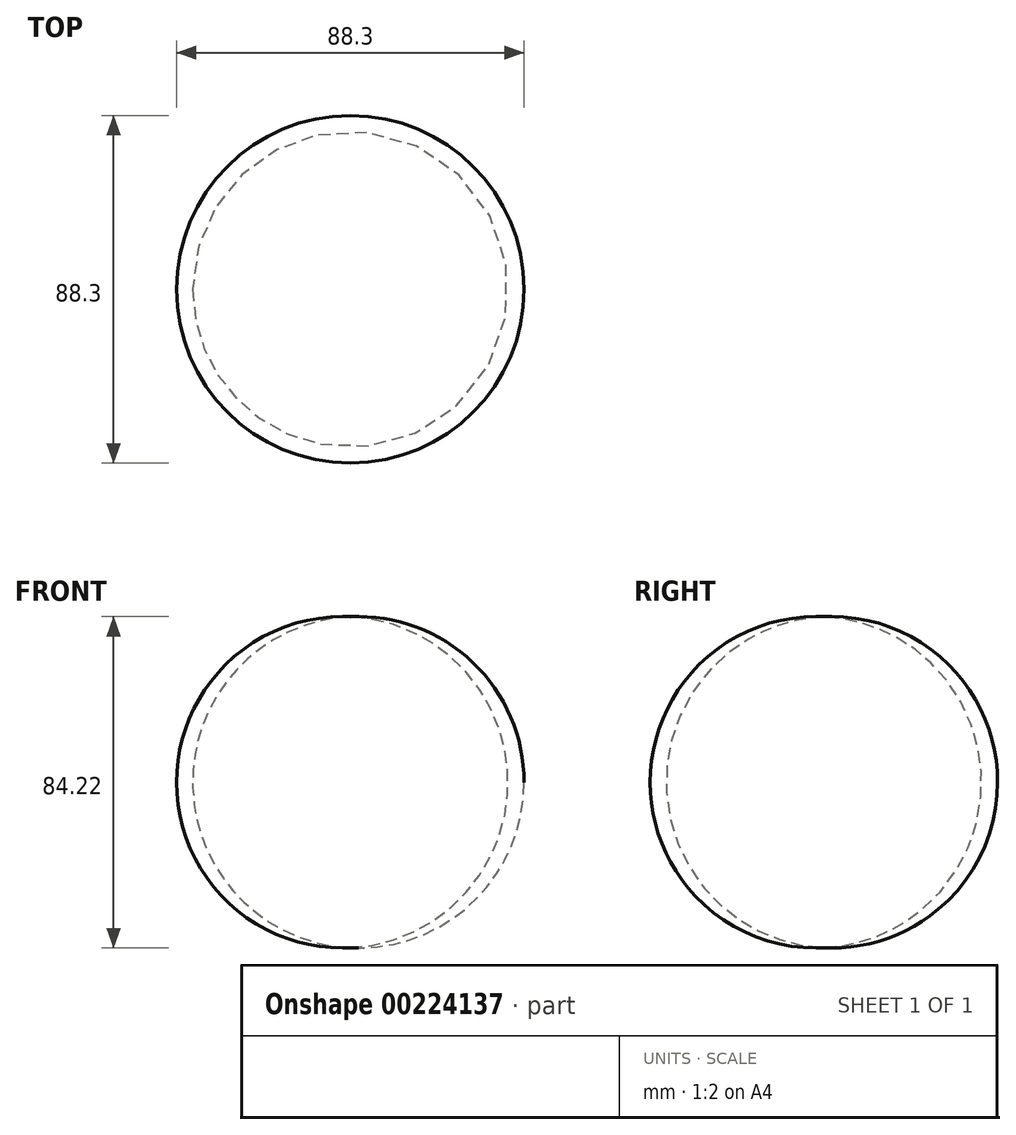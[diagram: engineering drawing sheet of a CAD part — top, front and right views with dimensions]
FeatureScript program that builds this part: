
annotation { "Feature Type Name" : "Feature", "Feature Type Description" : "" }
export const myFeature = defineFeature(function(context is Context, id is Id, definition is map)
    precondition{}
    {
        {
            var Q0;
            Q0=qCreatedBy(makeId("Front.planeOp"),FACE);
            var sketch = newSketch(context, id + "F0", { "sketchPlane" : qUnion([Q0])});
            skCircle(sketch, "E0", {"center": v(2.04, 0) * mm, "radius": 42.1 * mm});
            skLineSegment(sketch, "E1", {"start": v(0, 42.06) * mm, "end": v(0, -42.06) * mm});
            skSolve(sketch);
        }
        {
            var Q0;
            {var subQ0=sQuery(id+"F0.wireOp",EDGE,"E1");Q0=makeQuery(id+"F0.imprint","IMPRINT",FACE,{"disambiguationData":[TD([[makeQuery(id+"F0.imprint","IMPRINT",EDGE,{"derivedFrom":subQ0}),1.0]])]});}
            var Q1;
            Q1=sQuery(id+"F0.wireOp",EDGE,"E1");
            revolve(context, id + "F1", {"entities" : qUnion([Q0]), "axis" : qUnion([Q1]), "revolveType" : RevolveType.FULL});
        }
    });
